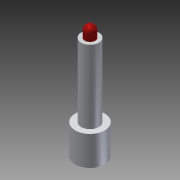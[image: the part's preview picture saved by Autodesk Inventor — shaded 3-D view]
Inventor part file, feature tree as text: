
AUTODESK INVENTOR PART (.ipt)
format: ipt  version: 2015 (Build 190159000, 159)  size: 95,744 bytes
history: native  units: mm
features: plane x3, sketch x3, extrude x3, fillet x1
ambient origin geometry x8: Origin, YZ Plane, XZ Plane, XY Plane, X Axis, Y Axis, Z Axis, Center Point
bodies: Solid1 (feature_tree)
feature tree (10):
  plane  "Work Plane1"
  sketch  "Sketch2"  dims[d3=50.0mm d4=30.0mm]
  extrude  "Extrusion2"  Depth=50.0mm
  extrude  "Extrusion3"  Depth=174.0mm TaperAngle=0.0deg
  plane  "Work Plane3"
  extrude  "Extrusion4"  Depth=9.0mm TaperAngle=0.0deg
  plane  "Work Plane2"
  sketch  "Sketch4"  dims[d9=18.0mm d10=20.0mm d11=0.0mm d13=9.0mm]
  fillet  "Fillet2"  Radius=9.0mm
  sketch  "Sketch3"  dims[d5=50.0mm d6=0.0mm d7=174.0mm d8=0.0mm]
